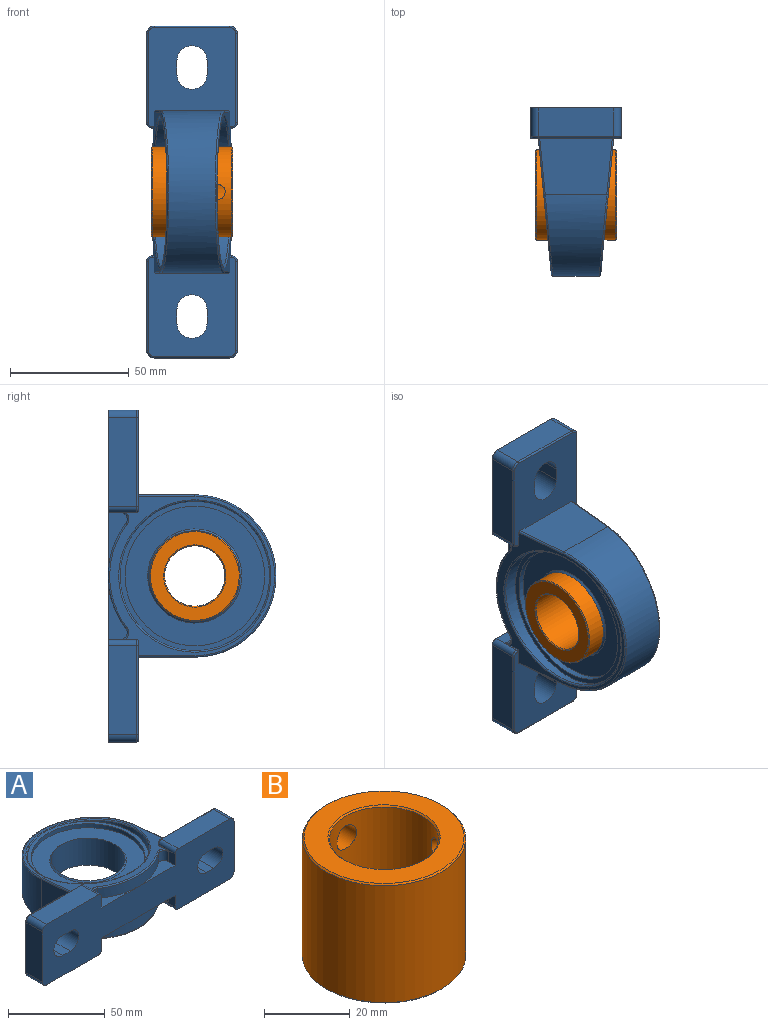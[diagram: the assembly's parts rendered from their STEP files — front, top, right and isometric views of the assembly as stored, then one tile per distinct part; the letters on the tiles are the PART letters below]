
ASSEMBLY  parts=2 mates=1
PART A: 92 faces, bbox 140.4x70.9x38.8 mm
  f0: bspline ~59.55x32.21mm, area 81.4mm2, adj f35,f47,f88,f89
  f1: bspline ~34.13x34.13mm, area 51.2mm2, adj f12,f34,f65,f66
  f2: bspline ~22.13x8.01mm, area 24.9mm2, adj f14,f35,f59,f60
  f3: cone r=19.81mm half-angle=45deg, axis (0,0,1), area 131.6mm2, adj f7,f49
  f4: cylinder r=29.37mm len=58.74mm, axis (0,0,-1), area 468.7mm2, adj f48,f49
  f5: cone r=19.05mm half-angle=45deg, axis (0,0,-1), area 131.6mm2, adj f7,f46
  f6: cylinder r=29.37mm len=58.74mm, axis (0,0,-1), area 468.7mm2, adj f45,f46
  f7: cylinder r=19.05mm len=38.1mm, axis (0,0,-1), area 2044.6mm2, adj f3,f5
  f8: plane 12.28x7.45mm, normal (-1,0,0), area 40.7mm2, adj f23,f28,f33,f35,f57,f58,f78
  f9: plane 12.28x7.45mm, normal (1,0,0), area 40.8mm2, adj f23,f27,f31,f34,f55,f67,f87
  f10: cylinder r=36.51mm len=44.19mm, axis (0,0,-1), area 292.7mm2, adj f26,f27,f30,f31,f68
  f11: plane 12.28x7.45mm, normal (-1,0,0), area 40.7mm2, adj f23,f26,f30,f34,f54,f69,f70
  f12: cylinder r=34.13mm len=68.26mm, axis (0,0,-1), area 2605.8mm2, adj f1,f13,f15,f62,f65
  f13: plane 30.47x23.81mm, normal (-1,0,0), area 671.3mm2, adj f12,f20,f63,f66
  f14: cylinder r=36.51mm len=44.19mm, axis (0,0,-1), area 309.4mm2, adj f2,f28,f29,f32,f33,f59
  f15: plane 30.47x23.81mm, normal (1,0,0), area 671.3mm2, adj f12,f25,f61,f64
  f16: plane 37.52x12.07mm, normal (0,0,-1), area 452.7mm2, adj f23,f50,f56,f81
  f17: plane 37.52x12.07mm, normal (0,0,1), area 452.7mm2, adj f23,f51,f55,f85
  f18: plane 37.52x12.07mm, normal (0,0,1), area 452.7mm2, adj f23,f53,f54,f72
  f19: plane 37.52x12.07mm, normal (0,0,-1), area 452.7mm2, adj f23,f52,f57,f76
  f20: plane 41.74x36.86mm, normal (0,1,0), area 1124.8mm2, adj f13,f34,f35,f36,f37,f38,f39,f63
  f21: plane 31.75x12.07mm, normal (-1,0,0), area 383.1mm2, adj f23,f50,f51,f83
  f22: plane 12.28x7.45mm, normal (1,0,0), area 40.7mm2, adj f23,f29,f32,f35,f56,f60,f79
  f23: plane 139.7x38.1mm, normal (0,-1,0), area 3891.4mm2, adj f8,f9,f11,f16,f17,f18,f19,f21
  f24: plane 31.75x12.07mm, normal (1,0,0), area 383.1mm2, adj f23,f52,f53,f74
  f25: plane 41.74x36.86mm, normal (0,1,0), area 1124.8mm2, adj f15,f34,f35,f40,f41,f42,f43,f61
  f26: plane 26.87x8.05mm, normal (0,0,1), area 88.5mm2, adj f10,f11,f23,f30
  f27: plane 26.87x8.05mm, normal (0,0,1), area 88.5mm2, adj f9,f10,f23,f31
  f28: plane 26.87x8.05mm, normal (0,0,-1), area 88.5mm2, adj f8,f14,f23,f33
  f29: plane 26.87x8.05mm, normal (0,0,-1), area 88.5mm2, adj f14,f22,f23,f32
  f30: cylinder r=2.97mm len=6.44mm, axis (0,0,1), area 41.6mm2, adj f10,f11,f26,f69
  f31: cylinder r=2.97mm len=6.44mm, axis (0,0,1), area 41.6mm2, adj f9,f10,f27,f67
  f32: cylinder r=2.97mm len=6.44mm, axis (0,0,-1), area 41.6mm2, adj f14,f22,f29,f60
  f33: cylinder r=2.97mm len=6.44mm, axis (0,0,-1), area 41.6mm2, adj f8,f14,f28,f58
  f34: plane 74.25x69.5mm, normal (0,0.1,1), area 582.9mm2, adj f1,f9,f11,f20,f25,f64,f65,f66
  f35: plane 74.25x69.5mm, normal (0,0.1,-1), area 601.7mm2, adj f0,f2,f8,f20,f22,f25,f58,f59
  f36: cylinder r=6.35mm len=12.7mm, axis (0,1,0), area 253.4mm2, adj f20,f23,f37,f39
  f37: plane 12.7x5.56mm, normal (0,0,1), area 70.6mm2, adj f20,f23,f36,f38
  f38: cylinder r=6.35mm len=12.7mm, axis (0,1,0), area 253.4mm2, adj f20,f23,f37,f39
  f39: plane 12.7x5.56mm, normal (0,0,-1), area 70.6mm2, adj f20,f23,f36,f38
  f40: cylinder r=6.35mm len=12.7mm, axis (0,1,0), area 253.4mm2, adj f23,f25,f41,f43
  f41: plane 12.7x5.56mm, normal (0,0,1), area 70.6mm2, adj f23,f25,f40,f42
  f42: cylinder r=6.35mm len=12.7mm, axis (0,1,0), area 253.4mm2, adj f23,f25,f41,f43
  f43: plane 12.7x5.56mm, normal (0,0,-1), area 70.6mm2, adj f23,f25,f40,f42
  f44: cylinder r=31.43mm len=62.87mm, axis (0,0,-1), area 0mm2, adj f45,f90
  f45: plane 62.96x62.96mm, normal (0,0,1), area 394.2mm2, adj f6,f44,f91
  f46: plane 58.74x58.74mm, normal (0,0,1), area 1476.6mm2, adj f5,f6
  f47: cylinder r=31.43mm len=62.87mm, axis (0,0,-1), area 466.6mm2, adj f0,f48,f88
  f48: plane 62.96x62.96mm, normal (0,0,-1), area 394.2mm2, adj f4,f47,f89
  f49: plane 58.74x58.74mm, normal (0,0,-1), area 1476.6mm2, adj f3,f4
  f50: cylinder r=3.17mm len=12.07mm, axis (0,-1,0), area 60.2mm2, adj f16,f21,f23,f82
  f51: cylinder r=3.17mm len=12.07mm, axis (0,1,0), area 60.2mm2, adj f17,f21,f23,f84
  f52: cylinder r=3.17mm len=12.07mm, axis (0,1,0), area 60.2mm2, adj f19,f23,f24,f75
  f53: cylinder r=3.17mm len=12.07mm, axis (0,-1,0), area 60.2mm2, adj f18,f23,f24,f73
  f54: cylinder r=2.29mm len=12.07mm, axis (0,1,0), area 43.3mm2, adj f11,f18,f23,f71
  f55: cylinder r=2.29mm len=12.07mm, axis (0,-1,0), area 43.3mm2, adj f9,f17,f23,f86
  f56: cylinder r=2.29mm len=12.07mm, axis (0,1,0), area 43.3mm2, adj f16,f22,f23,f80
  f57: cylinder r=2.29mm len=12.07mm, axis (0,-1,0), area 43.3mm2, adj f8,f19,f23,f77
  f58: bspline ~5.79x3.67mm, area 6.4mm2, adj f8,f33,f35,f59
  f59: bspline ~22.13x8.01mm, area 24.9mm2, adj f2,f14,f35,f58
  f60: bspline ~5.8x3.75mm, area 6.4mm2, adj f2,f22,f32,f35
  f61: cylinder r=0.64mm len=23.93mm, axis (0,1,0.1), area 23.9mm2, adj f15,f25,f35,f62
  f62: bspline ~68.26x34.11mm, area 102.3mm2, adj f12,f35,f61,f63
  f63: cylinder r=0.64mm len=23.93mm, axis (0,-1,-0.1), area 23.9mm2, adj f13,f20,f35,f62
  f64: cylinder r=0.64mm len=23.93mm, axis (0,-1,0.1), area 23.9mm2, adj f15,f25,f34,f65
  f65: bspline ~34.13x34.13mm, area 51.2mm2, adj f1,f12,f34,f64
  f66: cylinder r=0.64mm len=23.93mm, axis (0,1,-0.1), area 23.9mm2, adj f1,f13,f20,f34
  f67: bspline ~5.8x3.75mm, area 6.4mm2, adj f9,f31,f34,f68
  f68: bspline ~44.26x8.01mm, area 49.8mm2, adj f10,f34,f67,f69
  f69: bspline ~5.8x3.75mm, area 6.4mm2, adj f11,f30,f34,f68
  f70: cylinder r=0.64mm len=0.89mm, axis (0,0,1), area 0.9mm2, adj f11,f25,f34,f71
  f71: torus R=1.65mm, axis (0,-1,0), area 3.2mm2, adj f25,f54,f70,f72
  f72: cylinder r=0.64mm len=37.52mm, axis (1,0,0), area 37.4mm2, adj f18,f25,f71,f73
  f73: torus R=2.54mm, axis (0,-1,0), area 4.6mm2, adj f25,f53,f72,f74
  f74: cylinder r=0.64mm len=31.75mm, axis (0,0,-1), area 31.7mm2, adj f24,f25,f73,f75
  f75: torus R=2.54mm, axis (0,-1,0), area 4.6mm2, adj f25,f52,f74,f76
  f76: cylinder r=0.64mm len=37.52mm, axis (-1,0,0), area 37.4mm2, adj f19,f25,f75,f77
  f77: torus R=1.65mm, axis (0,-1,0), area 3.2mm2, adj f25,f57,f76,f78
  f78: cylinder r=0.64mm len=0.89mm, axis (0,0,-1), area 0.9mm2, adj f8,f25,f35,f77
  f79: cylinder r=0.64mm len=0.89mm, axis (0,0,-1), area 0.9mm2, adj f20,f22,f35,f80
  f80: torus R=1.65mm, axis (0,-1,0), area 3.2mm2, adj f20,f56,f79,f81
  f81: cylinder r=0.64mm len=37.52mm, axis (-1,0,0), area 37.4mm2, adj f16,f20,f80,f82
  f82: torus R=2.54mm, axis (0,-1,0), area 4.6mm2, adj f20,f50,f81,f83
  f83: cylinder r=0.64mm len=31.75mm, axis (0,0,-1), area 31.7mm2, adj f20,f21,f82,f84
  f84: torus R=2.54mm, axis (0,-1,0), area 4.6mm2, adj f20,f51,f83,f85
  f85: cylinder r=0.64mm len=37.52mm, axis (1,0,0), area 37.4mm2, adj f17,f20,f84,f86
  f86: torus R=1.65mm, axis (0,-1,0), area 3.2mm2, adj f20,f55,f85,f87
  f87: cylinder r=0.64mm len=0.89mm, axis (0,0,1), area 0.9mm2, adj f9,f20,f34,f86
  f88: bspline ~59.55x32.21mm, area 81.4mm2, adj f0,f35,f47,f89
  f89: bspline ~33.06x5.03mm, area 25.8mm2, adj f0,f35,f48,f88
  f90: bspline ~64.42x59.55mm, area 162.8mm2, adj f34,f44,f91
  f91: bspline ~33.06x5.03mm, area 25.8mm2, adj f34,f45,f90
PART B: 10 faces, bbox 38.1x38.1x34.1 mm
  f0: cone r=12.7mm half-angle=45deg, axis (0,0,1), area 43.6mm2, adj f6,f9
  f1: cone r=18.67mm half-angle=45deg, axis (0,0,-1), area 63.8mm2, adj f7,f9
  f2: cone r=13.08mm half-angle=45deg, axis (0,0,-1), area 43.6mm2, adj f6,f8
  f3: cone r=19.05mm half-angle=45deg, axis (0,0,1), area 63.8mm2, adj f7,f8
  f4: cylinder r=3.25mm len=8.81mm, axis (-0.87,0.5,0), area 129.7mm2, adj f6,f7
  f5: cylinder r=3.25mm len=6.5mm, axis (0,-1,0), area 129.7mm2, adj f6,f7
  f6: cylinder r=12.7mm len=33.37mm, axis (0,0,1), area 2598.3mm2, adj f0,f2,f4,f5
  f7: cylinder r=19.05mm len=38.1mm, axis (0,0,1), area 3927.6mm2, adj f1,f3,f4,f5
  f8: plane 37.34x37.34mm, normal (0,0,-1), area 557.4mm2, adj f2,f3
  f9: plane 37.34x37.34mm, normal (0,0,1), area 557.4mm2, adj f0,f1
PLACE A rot(axis=(0.71,0,-0.71),180deg) t=(375.97,-3953.17,-44.41)mm
PLACE B rot(axis=(0.71,0,0.71),180deg) t=(373.19,-3953.17,-44.41)mm
MATE revolute A.f4 <-> B.f0  axis (1,0,0) through (375.97,-3953.17,-44.41)mm
